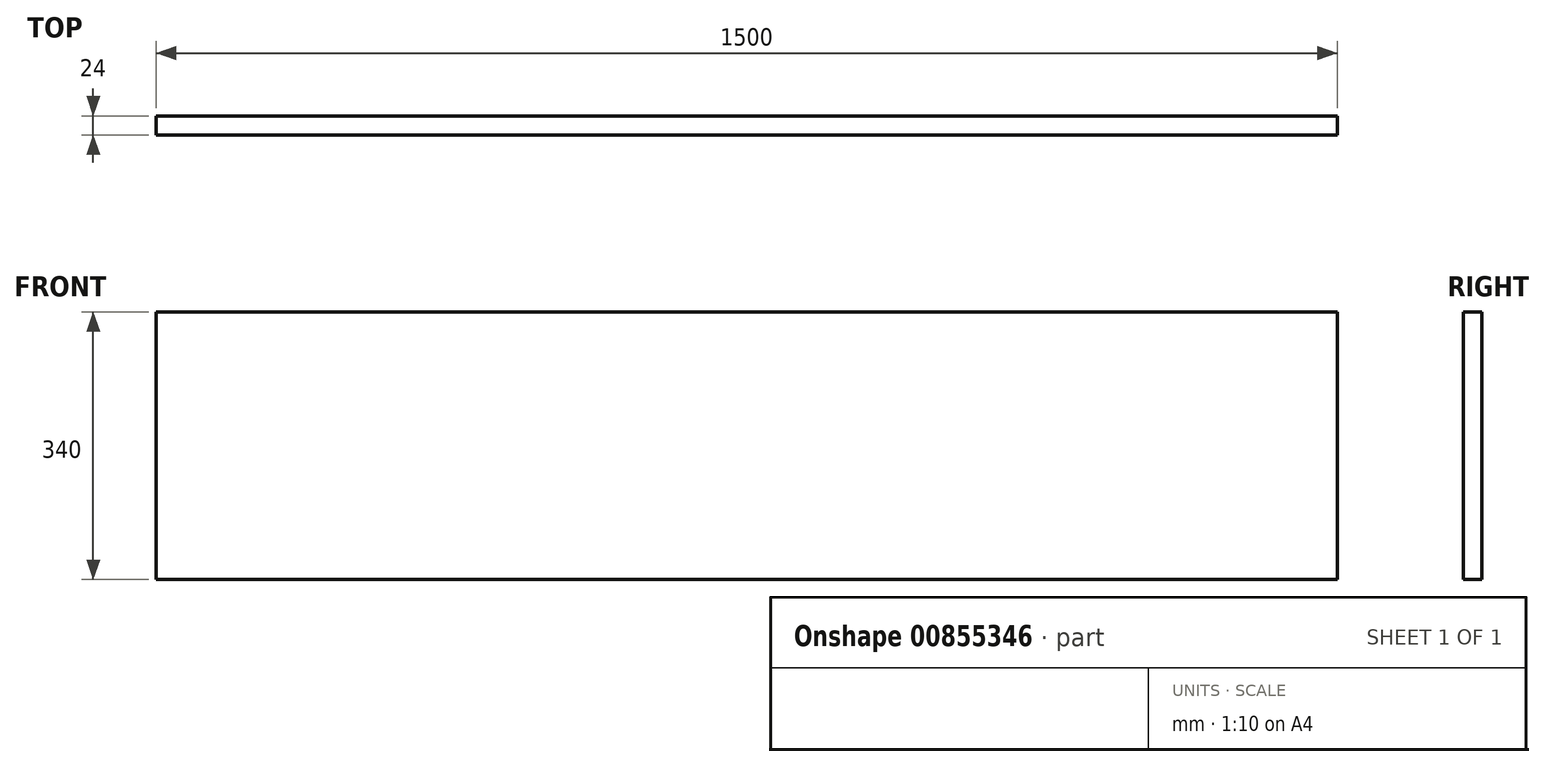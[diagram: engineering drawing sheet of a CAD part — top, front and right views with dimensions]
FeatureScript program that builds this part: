
annotation { "Feature Type Name" : "Feature", "Feature Type Description" : "" }
export const myFeature = defineFeature(function(context is Context, id is Id, definition is map)
    precondition{}
    {
        {
            var Q0;
            Q0=qCreatedBy(makeId("Front.planeOp"),FACE);
            var sketch = newSketch(context, id + "F0", { "sketchPlane" : qUnion([Q0])});
            skLineSegment(sketch, "E0.bottom", {"start": v(0, 0) * mm, "end": v(1500, 0) * mm});
            skLineSegment(sketch, "E0.top", {"start": v(0, 340) * mm, "end": v(1500, 340) * mm});
            skLineSegment(sketch, "E0.left", {"start": v(0, 0) * mm, "end": v(0, 340) * mm});
            skLineSegment(sketch, "E0.right", {"start": v(1500, 0) * mm, "end": v(1500, 340) * mm});
            skSolve(sketch);
        }
        {
            var Q0;
            Q0 = qSketchRegion(id + "F0", true);
            extrude(context, id + "F1", {"entities" : qUnion([Q0]), "depth" : 24 * mm, "offsetDistance" : 25 * mm});
        }
    });
